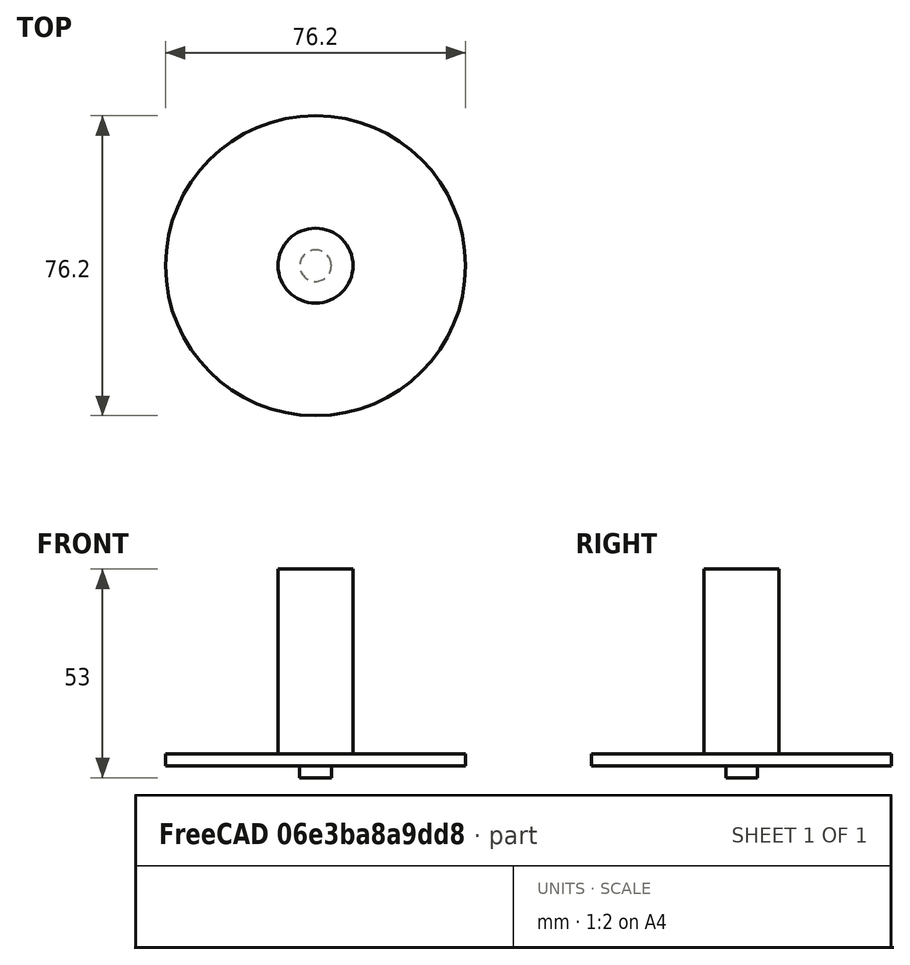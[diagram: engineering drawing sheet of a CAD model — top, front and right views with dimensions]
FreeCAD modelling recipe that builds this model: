
FCSTD DOCUMENT  (FreeCAD 0.22R37735 (Git))
Label: slittingsawnewreference
License: All rights reserved
LicenseURL: http://en.wikipedia.org/wiki/All_rights_reserved
objects: Sketcher::SketchObject×1, PartDesign::Revolution×1, App::FeaturePython×1, PartDesign::Body×1
note: 4 computed .brp shape members not serialized (recipe doc carries the construction recipe); baked Part::Feature solids carry a one-line shape summary decoded from their .brp

FEATURE [Sketcher::SketchObject] Sketch
  AttachmentSupport = -> [XZ_Plane]
  FullyConstrained = true
  MapMode = 5
  Placement = pos=(0,0,0) rot=(1,0,0;1.5708rad)
  Support = -> [XZ_Plane]
  expr: Constraints[18] = <<Attributes>>.CapDiameter
  expr: Constraints[20] = <<Attributes>>.CapHeight
  expr: Constraints[21] = <<Attributes>>.BladeThickness
  expr: Constraints[22] = <<Attributes>>.Diameter
  expr: Constraints[2] = <<Attributes>>.Length
  expr: Constraints[8] = <<Attributes>>.ShankDiameter
  sketch-geometry (11):
    g0: LineSegment StartX=0 StartY=50 StartZ=0 EndX=0 EndY=-3 EndZ=0
    g1: LineSegment StartX=9.525 StartY=50 StartZ=0 EndX=0 EndY=50 EndZ=0
    g2: LineSegment StartX=38.1 StartY=0 StartZ=0 EndX=-38.1 EndY=0 EndZ=0
    g3: LineSegment StartX=9.525 StartY=3 StartZ=0 EndX=38.1 EndY=3 EndZ=0
    g4: LineSegment StartX=9.525 StartY=50 StartZ=0 EndX=9.525 EndY=3 EndZ=0
    g5: LineSegment StartX=-9.525 StartY=50 StartZ=0 EndX=9.525 EndY=50 EndZ=0
    g6: LineSegment StartX=38.1 StartY=3 StartZ=0 EndX=38.1 EndY=0 EndZ=0
    g7: LineSegment StartX=38.1 StartY=0 StartZ=0 EndX=4 EndY=0 EndZ=0
    g8: LineSegment StartX=4 StartY=0 StartZ=0 EndX=4 EndY=-3 EndZ=0
    g9: LineSegment StartX=4 StartY=-3 StartZ=0 EndX=0 EndY=-3 EndZ=0
    g10: LineSegment StartX=-4 StartY=-3 StartZ=0 EndX=4 EndY=-3 EndZ=0
  constraints (30):
    c: Vertical(g0)
    c: Symmetric(g6,g2,g0)
    c: DistanceY(g6,g1) = 50
    c: Horizontal(g3)
    c: Vertical(g4)
    c: Coincident(g1,g4)
    c: Symmetric(g5,g5,g0)
    c: Coincident(g5,g1)
    c: DistanceX(g5,g5) = 19.05
    c: Coincident(g3,g4)
    c: Coincident(g3,g6)
    c: Vertical(g6)
    c: Coincident(g6,g7)
    c: Horizontal(g7)
    c: Coincident(g8,g9)
    c: Horizontal(g9)
    c: Vertical(g8)
    c: Coincident(g10,g8)
    c: DistanceX(g10,g10) = 8
    c: Symmetric(g10,g8,g-2)
    c: DistanceY(g8,g8) = 3
    c: DistanceY(g6,g6) = 3
    c: DistanceX(g2,g2) = 76.2
    c: Coincident(g7,g8)
    c: Coincident(g2,g6)
    c: Coincident(g0,g9)
    c: Coincident(g0,g1)
    c: Horizontal(g1)
    c: PointOnObject(g0,g-2)
    c: PointOnObject(g7,g-1)
FEATURE [PartDesign::Revolution] Revolution
  AllowMultiFace = false
  Angle = 360
  Angle2 = 60
  Axis = (0,2e-16,1)
  Base = (0,0,0)
  Placement = pos=(0,0,0) rot=(1,0,0;1.5708rad)
  Profile = -> Sketch
  ReferenceAxis = -> Sketch [V_Axis]
  Reversed = true
  Suppressed = false
  Type = 0
FEATURE [App::FeaturePython] PropertyBag  label="Attributes"  # WARN: FeaturePython — macro-defined, semantics opaque (R4)
  BladeThickness = 3
  CapDiameter = 8
  CapHeight = 3
  Chipload = 0
  CustomPropertyGroups = Shape | Attributes
  Diameter = 76.2
  Flutes = 0
  Length = 50
  Material = 0
  ShankDiameter = 19.05
FEATURE [PartDesign::Body] Body  label="SlittingSawNewReference"
  AllowCompound = false
  Group = -> [Sketch,Revolution,PropertyBag]
  Origin = -> Origin
  Tip = -> Revolution
